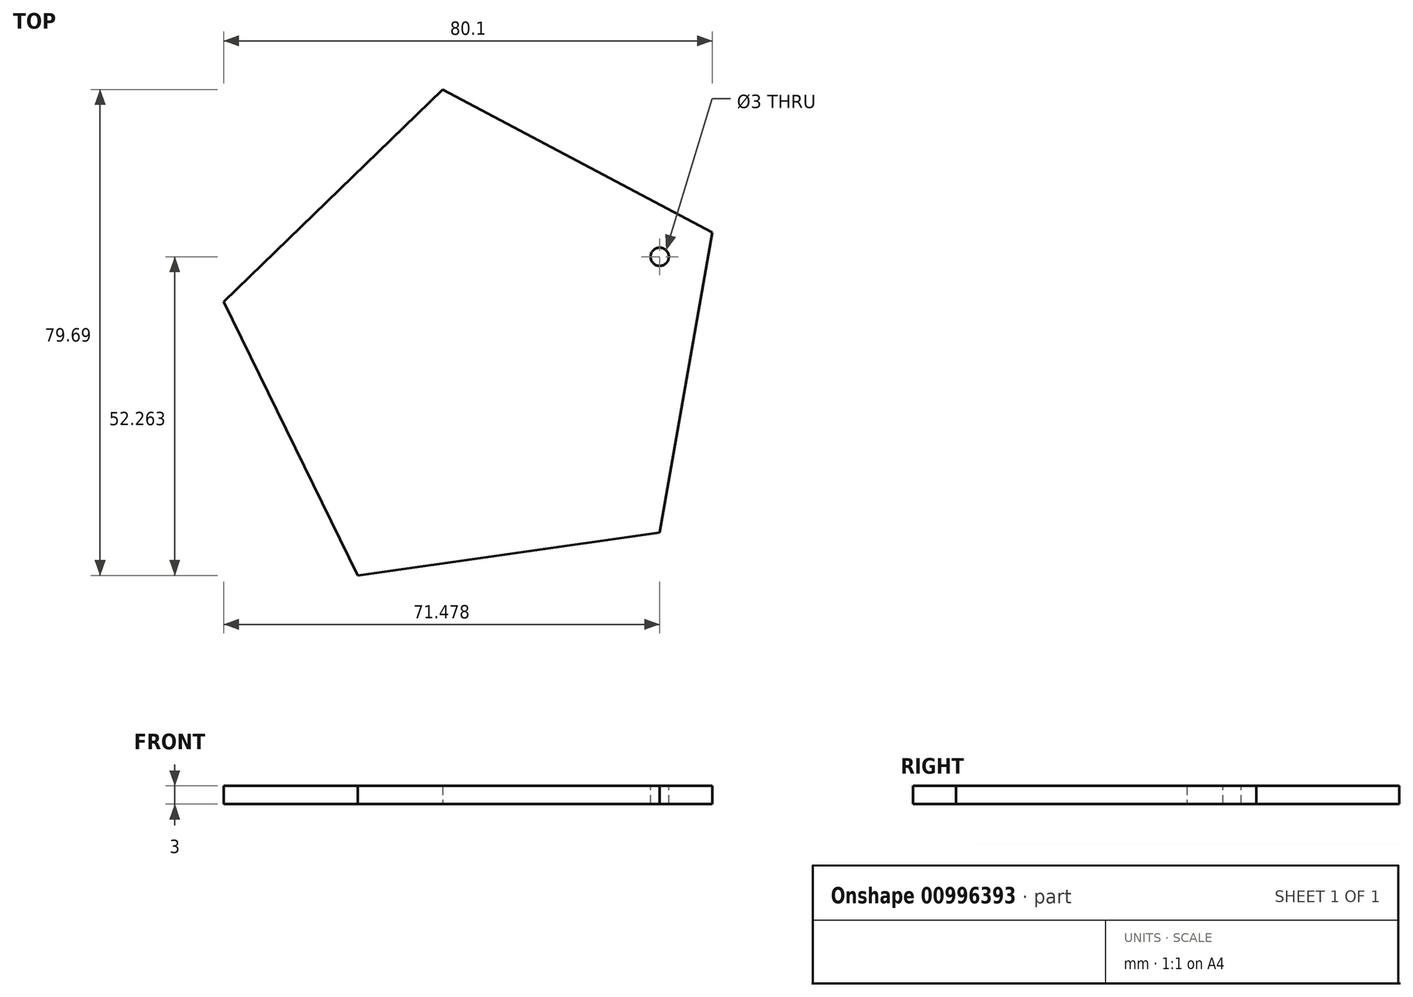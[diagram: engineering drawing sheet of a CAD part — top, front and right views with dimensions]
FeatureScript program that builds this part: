
annotation { "Feature Type Name" : "Feature", "Feature Type Description" : "" }
export const myFeature = defineFeature(function(context is Context, id is Id, definition is map)
    precondition{}
    {
        {
            var Q0;
            Q0=qCreatedBy(makeId("Top.planeOp"),FACE);
            var sketch = newSketch(context, id + "F0", { "sketchPlane" : qUnion([Q0])});
            skCircle(sketch, "E0.cCircle", {"center": v(-43.38, 50.33) * mm, "radius": 42.53 * mm, "construction": true});
            skLineSegment(sketch, "E0.0", {"start": v(-13.8, 19.77) * mm, "end": v(-63.3, 12.75) * mm});
            skLineSegment(sketch, "E0.1", {"start": v(-63.3, 12.75) * mm, "end": v(-85.28, 57.66) * mm});
            skLineSegment(sketch, "E0.2", {"start": v(-85.28, 57.66) * mm, "end": v(-49.35, 92.44) * mm});
            skLineSegment(sketch, "E0.3", {"start": v(-49.35, 92.44) * mm, "end": v(-5.18, 69.02) * mm});
            skLineSegment(sketch, "E0.4", {"start": v(-5.18, 69.02) * mm, "end": v(-13.8, 19.77) * mm});
            skSolve(sketch);
        }
        {
            var Q0;
            Q0 = qSketchRegion(id + "F0", true);
            extrude(context, id + "F1", {"entities" : qUnion([Q0]), "depth" : 3 * mm, "offsetDistance" : 25 * mm});
        }
        {
            var Q0;
            Q0=makeQuery(id+"F1.opExtrude","CAP_FACE",FACE,{"disambiguationData":[OSD([sQuery(id+"F0.wireOp",EDGE,"E0.0"),sQuery(id+"F0.wireOp",EDGE,"E0.1"),sQuery(id+"F0.wireOp",EDGE,"E0.2"),sQuery(id+"F0.wireOp",EDGE,"E0.3"),sQuery(id+"F0.wireOp",EDGE,"E0.4")])],"isStart":false});
            var sketch = newSketch(context, id + "F2", { "sketchPlane" : qUnion([Q0])});
            skCircle(sketch, "E1", {"center": v(-13.8, 65.01) * mm, "radius": 1.5 * mm});
            skSolve(sketch);
        }
        {
            var Q0;
            Q0 = qSketchRegion(id + "F2", true);
            extrude(context, id + "F3", {"entities" : qUnion([Q0]), "operationType" : NewBodyOperationType.REMOVE, "endBound" : BoundingType.THROUGH_ALL, "oppositeDirection" : true, "depth" : 3 * mm, "offsetDistance" : 25 * mm});
        }
    });
